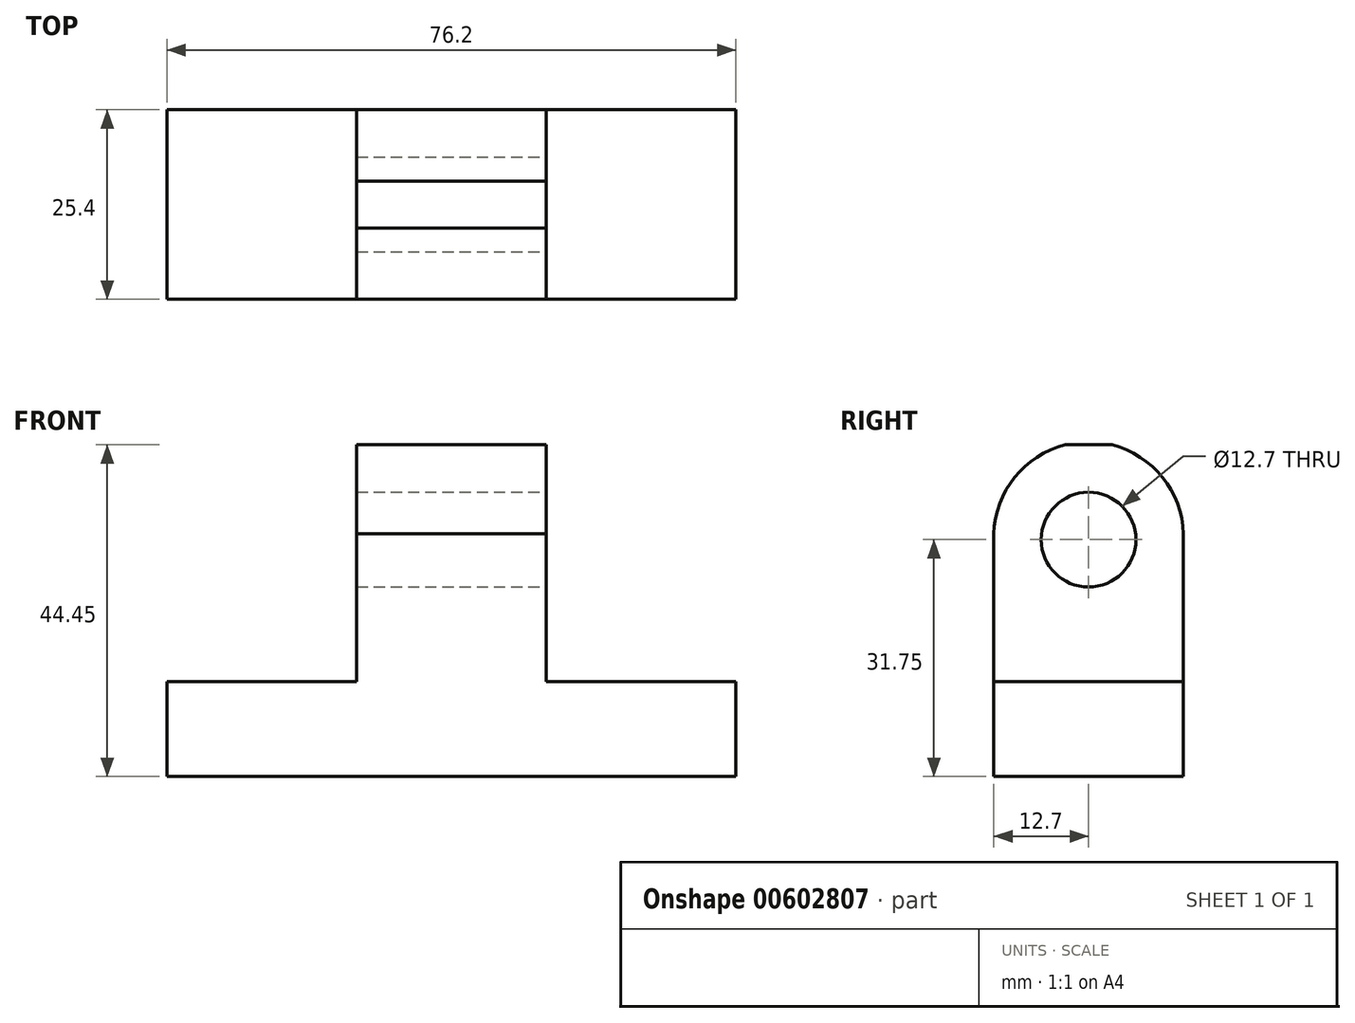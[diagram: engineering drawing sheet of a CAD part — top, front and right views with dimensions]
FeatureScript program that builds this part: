
annotation { "Feature Type Name" : "Feature", "Feature Type Description" : "" }
export const myFeature = defineFeature(function(context is Context, id is Id, definition is map)
    precondition{}
    {
        {
            var Q0;
            Q0=qCreatedBy(makeId("Front.planeOp"),FACE);
            var sketch = newSketch(context, id + "F0", { "sketchPlane" : qUnion([Q0])});
            skLineSegment(sketch, "E0", {"start": v(0, 0) * mm, "end": v(76.2, 0) * mm});
            skLineSegment(sketch, "E1", {"start": v(0, 0) * mm, "end": v(0, 12.7) * mm});
            skLineSegment(sketch, "E2", {"start": v(0, 12.7) * mm, "end": v(25.4, 12.7) * mm});
            skLineSegment(sketch, "E3", {"start": v(25.4, 12.7) * mm, "end": v(25.4, 44.45) * mm});
            skLineSegment(sketch, "E4", {"start": v(25.4, 44.45) * mm, "end": v(50.8, 44.45) * mm});
            skLineSegment(sketch, "E5", {"start": v(50.8, 44.45) * mm, "end": v(50.8, 12.7) * mm});
            skLineSegment(sketch, "E6", {"start": v(50.8, 12.7) * mm, "end": v(76.2, 12.7) * mm});
            skLineSegment(sketch, "E7", {"start": v(76.2, 12.7) * mm, "end": v(76.2, 0) * mm});
            skSolve(sketch);
        }
        {
            var Q0;
            Q0=makeQuery(id+"F0.imprint","IMPRINT",FACE,{"disambiguationData":[TD([[makeQuery(id+"F0.imprint","IMPRINT",EDGE,{"derivedFrom":sQuery(id+"F0.wireOp",EDGE,"E0")}),1.0]])]});
            extrude(context, id + "F1", {"entities" : qUnion([Q0]), "depth" : 25.4 * mm, "offsetDistance" : 25.4 * mm});
        }
        {
            var Q0;
            Q0=makeQuery(id+"F1.opExtrude","SWEPT_FACE",FACE,{"disambiguationData":[OSD([sQuery(id+"F0.wireOp",EDGE,"E5")])]});
            var sketch = newSketch(context, id + "F2", { "sketchPlane" : qUnion([Q0])});
            skCircle(sketch, "E8", {"center": v(-12.7, 31.75) * mm, "radius": 6.35 * mm});
            skArc(sketch, "E9", {"start": v(0, 31.75) * mm, "mid": v(-12.7, 44.84) * mm, "end": v(-25.4, 31.75) * mm});
            skSolve(sketch);
        }
        {
            var Q0;
            {var subQ0=sQuery(id+"F2.wireOp",EDGE,"E9");var subQ1=sQuery(id+"F0.wireOp",EDGE,"E5");var subQ2=makeQuery(id+"F1.opExtrude","CAP_EDGE",EDGE,{"disambiguationData":[OSD([subQ1])],"isStart":true});var subQ3=makeQuery(id+"F2.imprint","INTERSECT",VERTEX,{"disambiguationData":[OD(1.0)],"derivedFrom":[subQ2,subQ0]});Q0=makeQuery(id+"F2.imprint","IMPRINT",FACE,{"disambiguationData":[TD([[makeQuery(id+"F2.imprint","IMPRINT",EDGE,{"disambiguationData":[TD([[subQ3,-1.0]])],"derivedFrom":subQ0}),-1.0]])]});}
            var Q1;
            {var subQ0=sQuery(id+"F2.wireOp",EDGE,"E9");var subQ1=sQuery(id+"F0.wireOp",EDGE,"E5");var subQ4=makeQuery(id+"F1.opExtrude","CAP_EDGE",EDGE,{"disambiguationData":[OSD([subQ1])],"isStart":false});var subQ5=makeQuery(id+"F2.imprint","INTERSECT",VERTEX,{"disambiguationData":[OD(1.0)],"derivedFrom":[subQ4,subQ0]});Q1=makeQuery(id+"F2.imprint","IMPRINT",FACE,{"disambiguationData":[TD([[makeQuery(id+"F2.imprint","IMPRINT",EDGE,{"disambiguationData":[TD([[subQ5,1.0]])],"derivedFrom":subQ0}),-1.0]])]});}
            var Q2;
            Q2=makeQuery(id+"F2.imprint","IMPRINT",FACE,{"disambiguationData":[TD([[makeQuery(id+"F2.imprint","IMPRINT",EDGE,{"derivedFrom":sQuery(id+"F2.wireOp",EDGE,"E8")}),1.0]])]});
            extrude(context, id + "F3", {"entities" : qUnion([Q0, Q1, Q2]), "operationType" : NewBodyOperationType.REMOVE, "oppositeDirection" : true, "depth" : 25.4 * mm, "offsetDistance" : 25.4 * mm});
        }
    });
